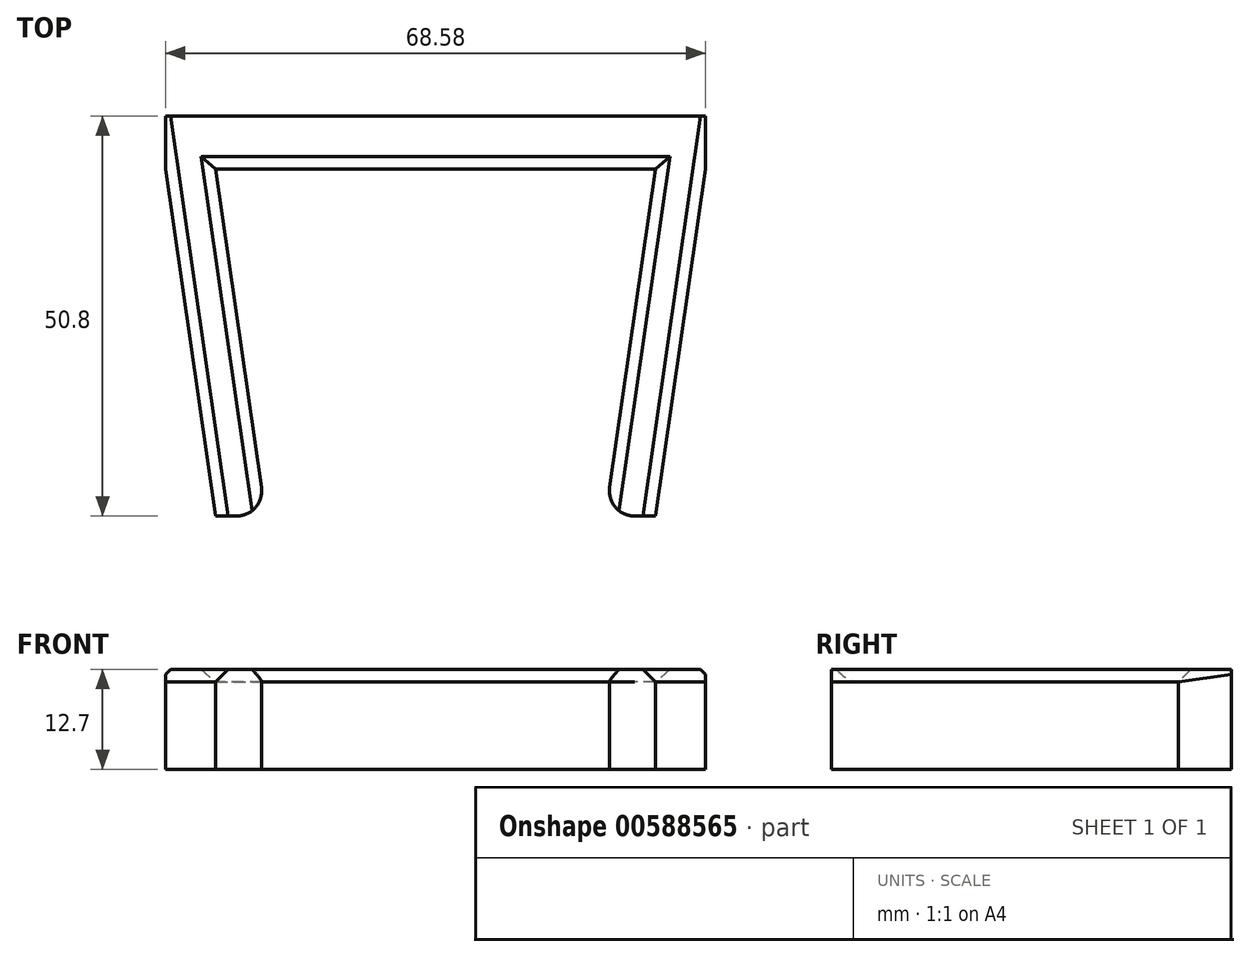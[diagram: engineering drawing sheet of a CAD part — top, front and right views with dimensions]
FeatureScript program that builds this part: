
annotation { "Feature Type Name" : "Feature", "Feature Type Description" : "" }
export const myFeature = defineFeature(function(context is Context, id is Id, definition is map)
    precondition{}
    {
        {
            var Q0;
            Q0=qCreatedBy(makeId("Top.planeOp"),FACE);
            var sketch = newSketch(context, id + "F0", { "sketchPlane" : qUnion([Q0])});
            skLineSegment(sketch, "E0.bottom", {"start": v(-34.3, 12.7) * mm, "end": v(34.3, 12.7) * mm});
            skLineSegment(sketch, "E0.top", {"start": v(-34.3, 5.95) * mm, "end": v(34.3, 5.95) * mm});
            skLineSegment(sketch, "E0.left", {"start": v(-34.3, 12.7) * mm, "end": v(-34.3, 5.95) * mm});
            skLineSegment(sketch, "E0.right", {"start": v(34.3, 12.7) * mm, "end": v(34.3, 5.95) * mm});
            skPoint(sketch, "E0.middle", {"position": v(0, 9.32) * mm});
            skLineSegment(sketch, "E1", {"start": v(-34.3, 5.95) * mm, "end": v(-27.94, -38.1) * mm});
            skLineSegment(sketch, "E2", {"start": v(-27.94, -38.1) * mm, "end": v(-21.6, -38.1) * mm});
            skLineSegment(sketch, "E3", {"start": v(-21.6, -38.1) * mm, "end": v(-27.94, 5.95) * mm});
            skLineSegment(sketch, "E4", {"start": v(34.3, 5.95) * mm, "end": v(27.94, -38.1) * mm});
            skLineSegment(sketch, "E5", {"start": v(27.94, -38.1) * mm, "end": v(21.59, -38.1) * mm});
            skLineSegment(sketch, "E6", {"start": v(21.59, -38.1) * mm, "end": v(27.94, 5.95) * mm});
            skSolve(sketch);
        }
        {
            var Q0;
            Q0 = qSketchRegion(id + "F0", true);
            extrude(context, id + "F1", {"entities" : qUnion([Q0]), "depth" : 12.7 * mm, "offsetDistance" : 25.4 * mm});
        }
        {
            var Q0;
            Q0=makeQuery(id+"F1.opExtrude","CAP_EDGE",EDGE,{"disambiguationData":[OSD([sQuery(id+"F0.wireOp",EDGE,"E3")])],"isStart":false});
            var Q1;
            Q1=makeQuery(id+"F1.opExtrude","CAP_EDGE",EDGE,{"disambiguationData":[OSD([sQuery(id+"F0.wireOp",EDGE,"E1")])],"isStart":false});
            var Q2;
            Q2=makeQuery(id+"F1.opExtrude","CAP_EDGE",EDGE,{"disambiguationData":[OSD([sQuery(id+"F0.wireOp",EDGE,"E0.top")])],"isStart":false});
            var Q3;
            Q3=makeQuery(id+"F1.opExtrude","CAP_EDGE",EDGE,{"disambiguationData":[OSD([sQuery(id+"F0.wireOp",EDGE,"E6")])],"isStart":false});
            var Q4;
            Q4=makeQuery(id+"F1.opExtrude","CAP_EDGE",EDGE,{"disambiguationData":[OSD([sQuery(id+"F0.wireOp",EDGE,"E4")])],"isStart":false});
            chamfer(context, id + "F2", {"entities" : qUnion([Q0, Q1, Q2, Q3, Q4]), "width" : 1.59 * mm, "tangentPropagation" : true});
        }
        {
            var Q0;
            Q0=makeQuery(id+"F1.opExtrude","SWEPT_EDGE",EDGE,{"disambiguationData":[OSD([sQuery(id+"F0.wireOp",EDGE,"E2"),sQuery(id+"F0.wireOp",EDGE,"E3")])]});
            var Q1;
            Q1=makeQuery(id+"F1.opExtrude","SWEPT_EDGE",EDGE,{"disambiguationData":[OSD([sQuery(id+"F0.wireOp",EDGE,"E5"),sQuery(id+"F0.wireOp",EDGE,"E6")])]});
            fillet(context, id + "F3", {"entities" : qUnion([Q0, Q1]), "radius" : 3.17 * mm, "tangentPropagation" : true, "allowEdgeOverflow" : false});
        }
    });
